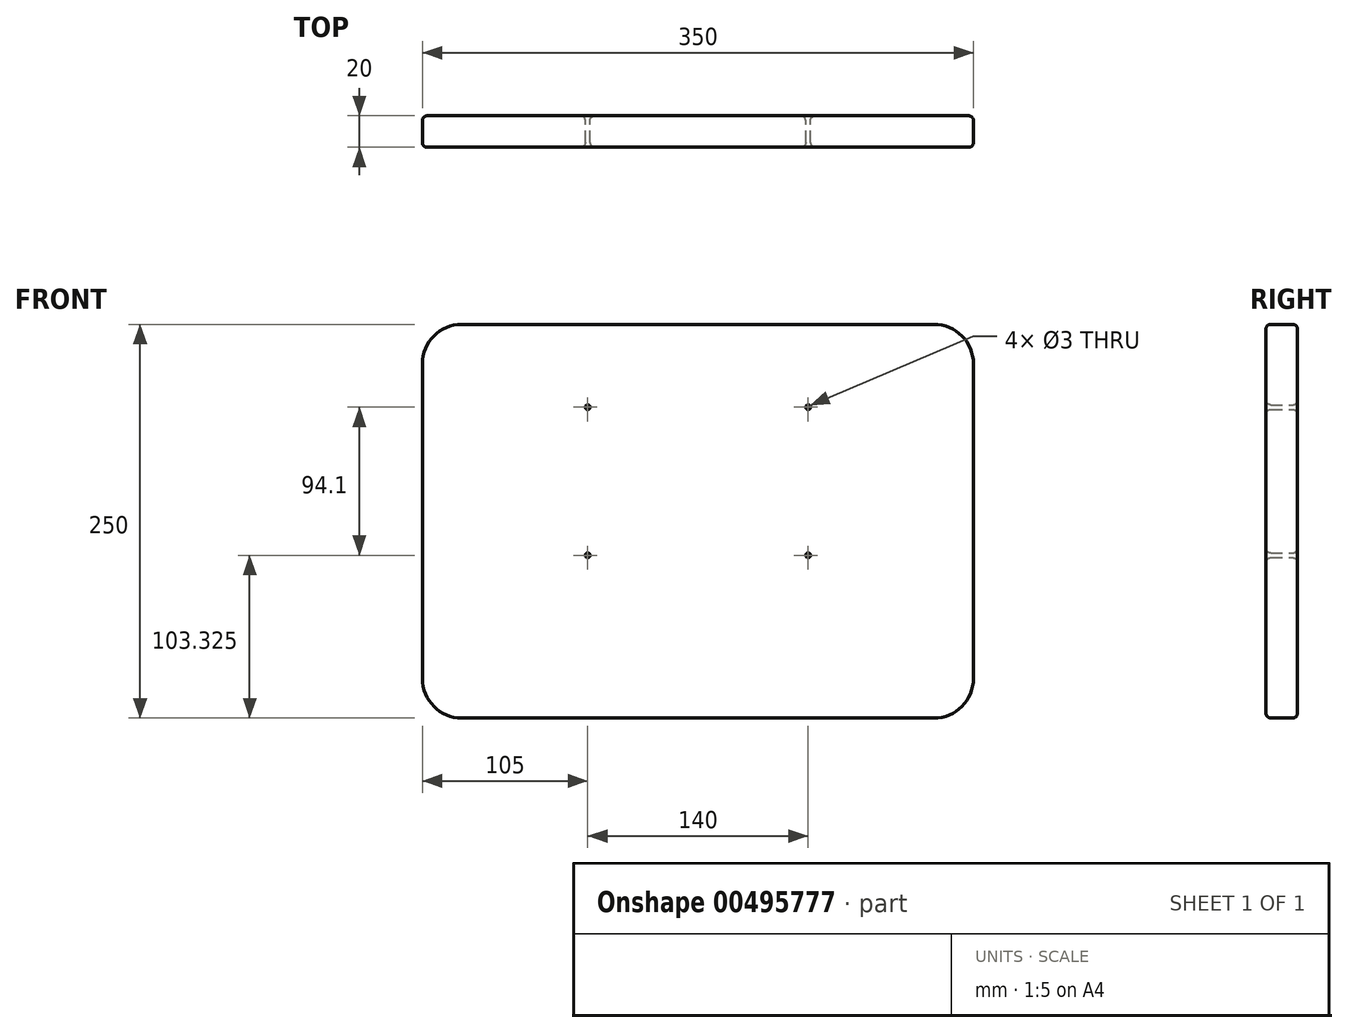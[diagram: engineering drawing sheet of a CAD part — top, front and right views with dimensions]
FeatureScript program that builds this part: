
annotation { "Feature Type Name" : "Feature", "Feature Type Description" : "" }
export const myFeature = defineFeature(function(context is Context, id is Id, definition is map)
    precondition{}
    {
        {
            var Q0;
            Q0=qCreatedBy(makeId("Front.planeOp"),FACE);
            var sketch = newSketch(context, id + "F0", { "sketchPlane" : qUnion([Q0])});
            skCircle(sketch, "E0", {"center": v(-70, 56.8) * mm, "radius": 1.5 * mm});
            skCircle(sketch, "E1", {"center": v(70, 56.8) * mm, "radius": 1.5 * mm});
            skLineSegment(sketch, "E2", {"start": v(0, -46.52) * mm, "end": v(-150, -46.52) * mm});
            skLineSegment(sketch, "E3", {"start": v(-150, 203.48) * mm, "end": v(0, 203.48) * mm});
            skLineSegment(sketch, "E4", {"start": v(-175, 178.48) * mm, "end": v(-175, -21.52) * mm});
            skPoint(sketch, "E5.visualSharp", {"position": v(-175, 203.48) * mm});
            skArc(sketch, "E5.filletArc", {"start": v(-150, 203.48) * mm, "mid": v(-167.68, 196.16) * mm, "end": v(-175, 178.48) * mm});
            skPoint(sketch, "E6.visualSharp", {"position": v(-175, -46.52) * mm});
            skArc(sketch, "E6.filletArc", {"start": v(-175, -21.52) * mm, "mid": v(-167.68, -39.2) * mm, "end": v(-150, -46.52) * mm});
            skCircle(sketch, "E7", {"center": v(-70, 150.9) * mm, "radius": 1.5 * mm});
            skCircle(sketch, "E8", {"center": v(70, 150.9) * mm, "radius": 1.5 * mm});
            skLineSegment(sketch, "E9", {"start": v(0, 216.3) * mm, "end": v(0, 180.85) * mm});
            skLineSegment(sketch, "E10.MirrorCS", {"start": v(150, 203.48) * mm, "end": v(0, 203.48) * mm});
            skArc(sketch, "E11.MirrorCS", {"start": v(150, 203.48) * mm, "mid": v(167.68, 196.16) * mm, "end": v(175, 178.48) * mm});
            skLineSegment(sketch, "E12.MirrorCS", {"start": v(175, 178.48) * mm, "end": v(175, -21.52) * mm});
            skLineSegment(sketch, "E13.MirrorCS", {"start": v(0, -46.52) * mm, "end": v(150, -46.52) * mm});
            skArc(sketch, "E14.MirrorCS", {"start": v(175, -21.52) * mm, "mid": v(167.68, -39.2) * mm, "end": v(150, -46.52) * mm});
            skLineSegment(sketch, "E15", {"start": v(0, 180.85) * mm, "end": v(0, 47.75) * mm});
            skLineSegment(sketch, "E16", {"start": v(-70, 150.9) * mm, "end": v(0, 150.9) * mm});
            skLineSegment(sketch, "E17", {"start": v(0, 150.9) * mm, "end": v(70, 150.9) * mm});
            skLineSegment(sketch, "E18", {"start": v(70, 56.8) * mm, "end": v(0, 56.8) * mm});
            skLineSegment(sketch, "E19", {"start": v(0, 56.8) * mm, "end": v(-70, 56.8) * mm});
            skPoint(sketch, "E20.endSnap0", {"position": v(-75, 203.48) * mm});
            skSolve(sketch);
        }
        {
            var Q0;
            Q0=makeQuery(id+"F0.imprint","IMPRINT",FACE,{"disambiguationData":[TD([[makeQuery(id+"F0.imprint","IMPRINT",EDGE,{"derivedFrom":sQuery(id+"F0.wireOp",EDGE,"E1")}),-1.0]])]});
            extrude(context, id + "F1", {"entities" : qUnion([Q0]), "endBound" : BoundingType.SYMMETRIC, "depth" : 20 * mm});
        }
        {
            var Q0;
            Q0=makeQuery(id+"F1.opExtrude","CAP_FACE",FACE,{"disambiguationData":[OSD([sQuery(id+"F0.wireOp",EDGE,"E0"),sQuery(id+"F0.wireOp",EDGE,"E1"),sQuery(id+"F0.wireOp",EDGE,"E2"),sQuery(id+"F0.wireOp",EDGE,"E3"),sQuery(id+"F0.wireOp",EDGE,"E4"),sQuery(id+"F0.wireOp",EDGE,"E5.filletArc"),sQuery(id+"F0.wireOp",EDGE,"E6.filletArc"),sQuery(id+"F0.wireOp",EDGE,"922498a0-1a24-4f7e-b6d6-d9dc9f0d9a5e0.MirrorCS"),sQuery(id+"F0.wireOp",EDGE,"cf168904-86be-4b7d-b9ed-cd1ad0f3df690.MirrorCS"),sQuery(id+"F0.wireOp",EDGE,"87c4811f-39fe-40a0-8f0f-8175311cea940.MirrorCS"),sQuery(id+"F0.wireOp",EDGE,"692f735f-b34a-43b6-8e04-aae55bc71afe0.MirrorCS"),sQuery(id+"F0.wireOp",EDGE,"b85d1574-dc12-461e-a240-8f775c5b91060.MirrorCS"),sQuery(id+"F0.wireOp",EDGE,"E7"),sQuery(id+"F0.wireOp",EDGE,"E8")])],"isStart":false});
            var Q1;
            Q1=makeQuery(id+"F1.opExtrude","CAP_FACE",FACE,{"disambiguationData":[OSD([sQuery(id+"F0.wireOp",EDGE,"E0"),sQuery(id+"F0.wireOp",EDGE,"E1"),sQuery(id+"F0.wireOp",EDGE,"E2"),sQuery(id+"F0.wireOp",EDGE,"E3"),sQuery(id+"F0.wireOp",EDGE,"E4"),sQuery(id+"F0.wireOp",EDGE,"E5.filletArc"),sQuery(id+"F0.wireOp",EDGE,"E6.filletArc"),sQuery(id+"F0.wireOp",EDGE,"922498a0-1a24-4f7e-b6d6-d9dc9f0d9a5e0.MirrorCS"),sQuery(id+"F0.wireOp",EDGE,"cf168904-86be-4b7d-b9ed-cd1ad0f3df690.MirrorCS"),sQuery(id+"F0.wireOp",EDGE,"87c4811f-39fe-40a0-8f0f-8175311cea940.MirrorCS"),sQuery(id+"F0.wireOp",EDGE,"692f735f-b34a-43b6-8e04-aae55bc71afe0.MirrorCS"),sQuery(id+"F0.wireOp",EDGE,"b85d1574-dc12-461e-a240-8f775c5b91060.MirrorCS"),sQuery(id+"F0.wireOp",EDGE,"E7"),sQuery(id+"F0.wireOp",EDGE,"E8")])],"isStart":true});
            fillet(context, id + "F2", {"entities" : qUnion([Q0, Q1]), "radius" : 3 * mm, "tangentPropagation" : true, "allowEdgeOverflow" : false});
        }
    });
